# Revit family: Poppin - Pitch Seatings 123
name_source: partatom
category: Furniture
revit_build: Autodesk Revit 2017 (Build: 20160225_1515(x64)
units: mm (PartAtom-declared; Revit-internal decimal feet)

## family parameters
Always vertical = Yes
Cut with Voids When Loaded = No
OmniClass Number = 23.40.20.00
OmniClass Title = General Furniture and Specialties
Room Calculation Point = No
Shared = Yes
Work Plane-Based = No

## types (10) — shared parameters
Assembly Code = E2020200
Catalog Code = POP
Depth = 23 7/16"
Height = 31 3/16"
Lead Time URL = https://www.poppin.com
Manufacturer = Poppin
Manufacturer Code = POP
Manufacturer URL = https://www.poppin.com
Product URL = https://www.poppin.com
Warranty URL = https://www.poppin.com
Width = 25 15/16"

## per-type parameters (varying)
| type | Description | Meeting Chair | Product number | Sled Chair |
| 107745 - Meeting Chair - Chord - Black | Poppin - Pitch Meeting Chair - Chord - Black | Yes | 107745 | No |
| 107746 - Meeting Chair - Chord - White | Poppin - Pitch Meeting Chair - Chord - White | Yes | 107746 | No |
| 106656 - Meeting Chair - Medley Blue | Poppin - Pitch Meeting Chair - Medley Blue | Yes | 106656 | No |
| 106657 - Meeting Chair - Medley Dark Blue | Poppin - Pitch Meeting Chair - Medley Dark Blue | Yes | 106657 | No |
| 106658 - Meeting Chair - Medley Dark Gray | Poppin - Pitch Meeting Chair - Medley Dark Gray | Yes | 106658 | No |
| 106659 - Meeting Chair - Medley Gray | Poppin - Pitch Meeting Chair - Medley Gray | Yes | 106659 | No |
| 106660 - Sled Chair - Blue | Poppin - Pitch Sled Chair - Blue | No | 106660 | Yes |
| 106661 - Sled Chair - Dark Blue | Poppin - Pitch Sled Chair - Dark Blue | No | 106661 | Yes |
| 106662 - Sled Chair - Dark Gray | Poppin - Pitch Sled Chair - Dark Gray | No | 106662 | Yes |
| 106663 - Sled Chair - Gray | Poppin - Pitch Sled Chair - Gray | No | 106663 | Yes |

## geometry (parser evidence)
native form markers: Sweep x10
no freeform markers — native parametric forms only
